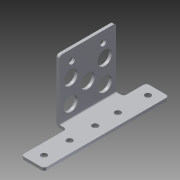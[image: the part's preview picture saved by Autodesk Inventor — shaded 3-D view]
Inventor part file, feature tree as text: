
AUTODESK INVENTOR PART (.ipt)
format: ipt  version: 2013 (Build 170138000, 138)  size: 251,392 bytes
history: native  units: in
note: dims shown in document units (in); Inventor stores cm internally (conversion verified against a paired STEP export)
features: sheet_metal_op x4, other x4, sketch x3, chamfer x1, reference x1
ambient origin geometry x8: Origin, YZ Plane, XZ Plane, XY Plane, X Axis, Y Axis, Z Axis, Center Point
bodies: Solid1 (feature_tree)
feature tree (13):
  sheet_metal_op  "Face1"
  sheet_metal_op  "Flange1"
  chamfer  "Corner Round1"
  sketch  "Sketch1"  dims[d0=1.0in]
  other  "Plate1"
  sketch  "Sketch2"  dims[d1=5.5in]
  other  "Plate2"
  sheet_metal_op  "Bend1"
  sheet_metal_op  "Corner1"
  sketch  "Sketch3"  dims[d2=0.5in d3=1.125in d4=1.125in d5=1.0in d6=1.325in d7=0.26in d8=2.5in d9=0.454in d10=2.0in d11=0.125in d12=0.125in d13=0.0625in d14=0.25in d15=0.125in d16=2.75in d17=90.0deg d18=0.05in d19=0.5in d20=0.125in d21=0.125in d22=0.125in d23=0.266in d25=0.266in d26=0.125in d27=0.0in d28=0.625in d29=0.7874in d31=1.0in d32=0.7874in d34=1.5in d37=0.5in d38=0.625in]
  reference  "Reference1"
  other  "Cut1"
  other  "Definition1"
